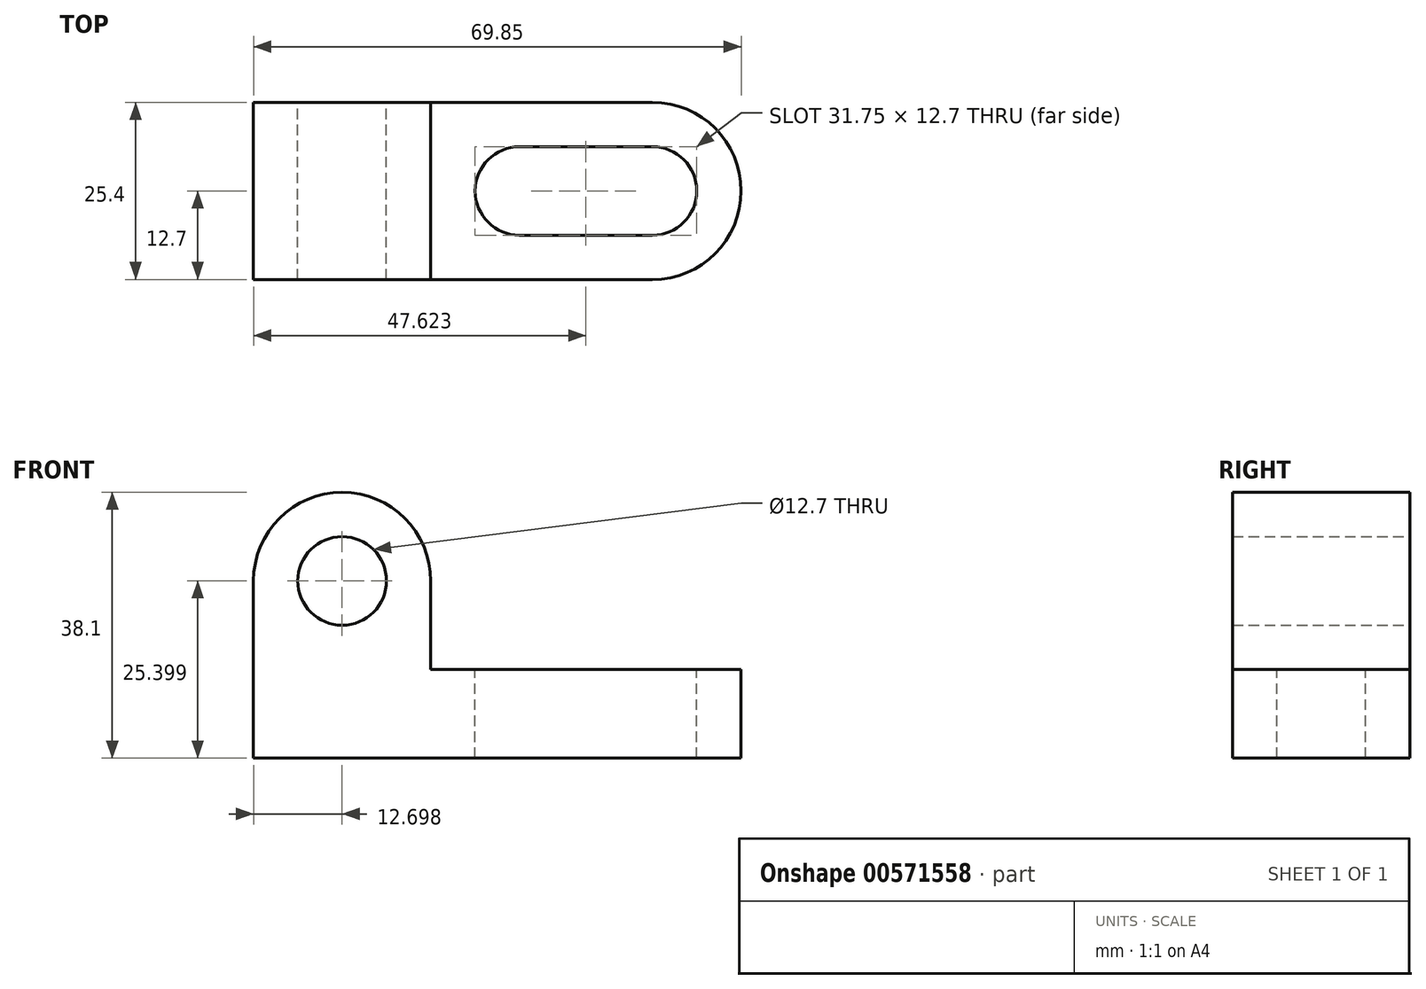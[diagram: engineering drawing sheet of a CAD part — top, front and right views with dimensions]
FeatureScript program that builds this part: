
annotation { "Feature Type Name" : "Feature", "Feature Type Description" : "" }
export const myFeature = defineFeature(function(context is Context, id is Id, definition is map)
    precondition{}
    {
        {
            var Q0;
            Q0=qCreatedBy(makeId("Front.planeOp"),FACE);
            var sketch = newSketch(context, id + "F0", { "sketchPlane" : qUnion([Q0])});
            skLineSegment(sketch, "E0", {"start": v(-45.13, 37.44) * mm, "end": v(-19.73, 37.44) * mm});
            skLineSegment(sketch, "E1", {"start": v(-19.73, 37.44) * mm, "end": v(-19.73, 24.74) * mm});
            skLineSegment(sketch, "E2", {"start": v(-19.73, 24.74) * mm, "end": v(12.02, 24.74) * mm});
            skLineSegment(sketch, "E3", {"start": v(12.02, 24.74) * mm, "end": v(12.02, 12.04) * mm});
            skLineSegment(sketch, "E4", {"start": v(12.02, 12.04) * mm, "end": v(-45.13, 12.04) * mm});
            skLineSegment(sketch, "E5", {"start": v(-45.13, 12.04) * mm, "end": v(-45.13, 37.44) * mm});
            skArc(sketch, "E6", {"start": v(-19.73, 37.44) * mm, "mid": v(-32.43, 50.14) * mm, "end": v(-45.13, 37.44) * mm});
            skCircle(sketch, "E7", {"center": v(-32.43, 37.44) * mm, "radius": 6.35 * mm});
            skSolve(sketch);
        }
        {
            var Q0;
            Q0 = qSketchRegion(id + "F0", true);
            extrude(context, id + "F1", {"entities" : qUnion([Q0]), "depth" : 25.4 * mm, "offsetDistance" : 25.4 * mm});
        }
        {
            var Q0;
            Q0=makeQuery(id+"F1.opExtrude","SWEPT_FACE",FACE,{"disambiguationData":[OSD([sQuery(id+"F0.wireOp",EDGE,"E2")])]});
            var sketch = newSketch(context, id + "F2", { "sketchPlane" : qUnion([Q0])});
            skArc(sketch, "E8", {"start": v(12.02, -25.4) * mm, "mid": v(24.72, -12.7) * mm, "end": v(12.02, 0) * mm});
            skSolve(sketch);
        }
        {
            var Q0;
            Q0=makeQuery(id+"F2.imprint","IMPRINT",FACE,{"disambiguationData":[TD([[makeQuery(id+"F2.imprint","IMPRINT",EDGE,{"derivedFrom":sQuery(id+"F2.wireOp",EDGE,"E8")}),1.0]])]});
            extrude(context, id + "F3", {"entities" : qUnion([Q0]), "operationType" : NewBodyOperationType.ADD, "oppositeDirection" : true, "depth" : 12.7 * mm, "offsetDistance" : 25.4 * mm});
        }
        {
            var Q0;
            {var subQ0=sQuery(id+"F0.wireOp",EDGE,"E2");Q0=makeQuery(id+"F3.boolean.opBoolean","MERGE",FACE,{"derivedFrom":[makeQuery(id+"F1.opExtrude","SWEPT_FACE",FACE,{"disambiguationData":[OSD([subQ0])]}),makeQuery(id+"F3.opExtrude","CAP_FACE",FACE,{"disambiguationData":[OSD([subQ0,sQuery(id+"F0.wireOp",EDGE,"E3"),sQuery(id+"F2.wireOp",EDGE,"E8")])],"isStart":true})]});}
            var sketch = newSketch(context, id + "F4", { "sketchPlane" : qUnion([Q0])});
            skLineSegment(sketch, "E9", {"start": v(-7.03, -6.35) * mm, "end": v(12.02, -6.35) * mm});
            skLineSegment(sketch, "E10", {"start": v(12.02, -6.35) * mm, "end": v(12.02, -19.05) * mm});
            skLineSegment(sketch, "E11", {"start": v(12.02, -19.05) * mm, "end": v(-7.03, -19.05) * mm});
            skLineSegment(sketch, "E12", {"start": v(-7.03, -19.05) * mm, "end": v(-7.03, -6.35) * mm});
            skArc(sketch, "E13", {"start": v(12.02, -19.05) * mm, "mid": v(18.37, -12.7) * mm, "end": v(12.02, -6.35) * mm});
            skArc(sketch, "E14", {"start": v(-7.03, -6.35) * mm, "mid": v(-13.38, -12.7) * mm, "end": v(-7.03, -19.05) * mm});
            skSolve(sketch);
        }
        {
            var Q0;
            Q0 = qSketchRegion(id + "F4", true);
            extrude(context, id + "F5", {"entities" : qUnion([Q0]), "operationType" : NewBodyOperationType.REMOVE, "oppositeDirection" : true, "depth" : 25.4 * mm, "offsetDistance" : 25.4 * mm});
        }
    });
